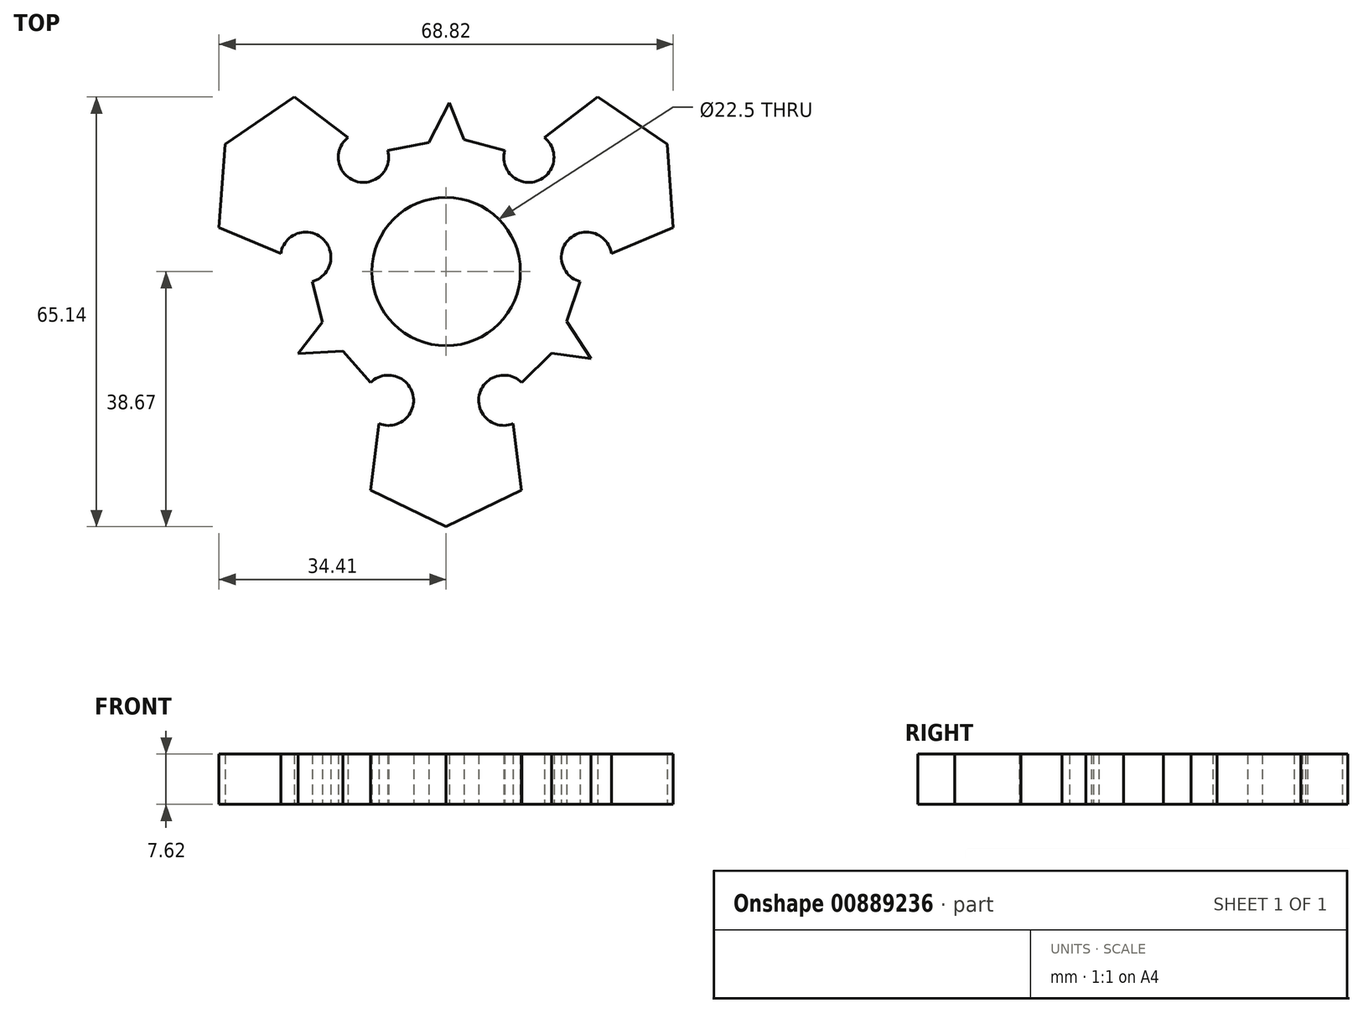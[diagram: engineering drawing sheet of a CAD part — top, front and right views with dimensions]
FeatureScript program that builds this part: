
annotation { "Feature Type Name" : "Feature", "Feature Type Description" : "" }
export const myFeature = defineFeature(function(context is Context, id is Id, definition is map)
    precondition{}
    {
        {
            var Q0;
            Q0=qCreatedBy(makeId("Top.planeOp"),FACE);
            var sketch = newSketch(context, id + "F0", { "sketchPlane" : qUnion([Q0])});
            skCircle(sketch, "E0", {"center": v(0, 0) * mm, "radius": 11.25 * mm});
            skCircle(sketch, "E1", {"center": v(0, 0) * mm, "radius": 13.97 * mm});
            skLineSegment(sketch, "E2", {"start": v(-10.16, -23.05) * mm, "end": v(-11.43, -33.13) * mm});
            skLineSegment(sketch, "E3", {"start": v(-11.43, -33.13) * mm, "end": v(0, -38.67) * mm});
            skArc(sketch, "E4", {"start": v(-10.16, -23.05) * mm, "mid": v(-5.02, -18.74) * mm, "end": v(-11.45, -16.84) * mm});
            skLineSegment(sketch, "E5.MirrorCS", {"start": v(11.43, -33.13) * mm, "end": v(0, -38.67) * mm});
            skLineSegment(sketch, "E6.MirrorCS", {"start": v(10.16, -23.05) * mm, "end": v(11.43, -33.13) * mm});
            skArc(sketch, "E7.MirrorCS", {"start": v(10.16, -23.05) * mm, "mid": v(5.02, -18.74) * mm, "end": v(11.45, -16.84) * mm});
            skLineSegment(sketch, "E8.1.0", {"start": v(25.05, 2.73) * mm, "end": v(34.41, 6.67) * mm});
            skArc(sketch, "E8.1.1", {"start": v(25.05, 2.73) * mm, "mid": v(18.74, 5.03) * mm, "end": v(20.3, -1.5) * mm});
            skLineSegment(sketch, "E8.1.2", {"start": v(34.41, 6.67) * mm, "end": v(33.49, 19.34) * mm});
            skLineSegment(sketch, "E8.1.3", {"start": v(22.98, 26.47) * mm, "end": v(33.49, 19.34) * mm});
            skLineSegment(sketch, "E8.1.4", {"start": v(14.89, 20.33) * mm, "end": v(22.98, 26.47) * mm});
            skArc(sketch, "E8.1.5", {"start": v(14.89, 20.33) * mm, "mid": v(13.72, 13.71) * mm, "end": v(8.85, 18.34) * mm});
            skLineSegment(sketch, "E8.2.0", {"start": v(-14.89, 20.33) * mm, "end": v(-22.98, 26.47) * mm});
            skArc(sketch, "E8.2.1", {"start": v(-14.89, 20.33) * mm, "mid": v(-13.72, 13.71) * mm, "end": v(-8.85, 18.34) * mm});
            skLineSegment(sketch, "E8.2.2", {"start": v(-22.98, 26.47) * mm, "end": v(-33.49, 19.34) * mm});
            skLineSegment(sketch, "E8.2.3", {"start": v(-34.41, 6.67) * mm, "end": v(-33.49, 19.34) * mm});
            skLineSegment(sketch, "E8.2.4", {"start": v(-25.05, 2.73) * mm, "end": v(-34.41, 6.67) * mm});
            skArc(sketch, "E8.2.5", {"start": v(-25.05, 2.73) * mm, "mid": v(-18.74, 5.03) * mm, "end": v(-20.3, -1.5) * mm});
            skLineSegment(sketch, "E9", {"start": v(-11.45, -16.84) * mm, "end": v(-15.65, -12.07) * mm});
            skLineSegment(sketch, "E10", {"start": v(-20.3, -1.5) * mm, "end": v(-18.72, -7.65) * mm});
            skLineSegment(sketch, "E11", {"start": v(-15.65, -12.07) * mm, "end": v(-22.43, -12.42) * mm});
            skLineSegment(sketch, "E12", {"start": v(-22.43, -12.42) * mm, "end": v(-18.72, -7.65) * mm});
            skLineSegment(sketch, "E13.1.0", {"start": v(11.45, -16.84) * mm, "end": v(15.99, -12.4) * mm});
            skLineSegment(sketch, "E13.1.1", {"start": v(21.97, -13.22) * mm, "end": v(15.99, -12.4) * mm});
            skLineSegment(sketch, "E13.1.2", {"start": v(18.28, -7.52) * mm, "end": v(21.97, -13.22) * mm});
            skLineSegment(sketch, "E13.1.3", {"start": v(20.3, -1.5) * mm, "end": v(18.28, -7.52) * mm});
            skLineSegment(sketch, "E13.2.0", {"start": v(8.85, 18.34) * mm, "end": v(2.74, 20.04) * mm});
            skLineSegment(sketch, "E13.2.1", {"start": v(0.46, 25.63) * mm, "end": v(2.74, 20.04) * mm});
            skLineSegment(sketch, "E13.2.2", {"start": v(-2.63, 19.59) * mm, "end": v(0.46, 25.63) * mm});
            skLineSegment(sketch, "E13.2.3", {"start": v(-8.85, 18.34) * mm, "end": v(-2.63, 19.59) * mm});
            skLineSegment(sketch, "E14", {"start": v(-3.78, -27.6) * mm, "end": v(-3.78, -33.65) * mm});
            skLineSegment(sketch, "E15", {"start": v(-3.78, -33.65) * mm, "end": v(1.9, -27.96) * mm});
            skLineSegment(sketch, "E16", {"start": v(1.9, -27.96) * mm, "end": v(3.23, -33.65) * mm});
            skSolve(sketch);
        }
        {
            var Q0;
            Q0=makeQuery(id+"F0.imprint","IMPRINT",FACE,{"disambiguationData":[TD([[makeQuery(id+"F0.imprint","IMPRINT",EDGE,{"derivedFrom":sQuery(id+"F0.wireOp",EDGE,"E1")}),-1.0]])]});
            var Q1;
            Q1=makeQuery(id+"F0.imprint","IMPRINT",FACE,{"disambiguationData":[TD([[makeQuery(id+"F0.imprint","IMPRINT",EDGE,{"derivedFrom":sQuery(id+"F0.wireOp",EDGE,"E0")}),-1.0]])]});
            extrude(context, id + "F1", {"entities" : qUnion([Q0, Q1]), "depth" : 7.62 * mm, "offsetDistance" : 25.4 * mm});
        }
    });
